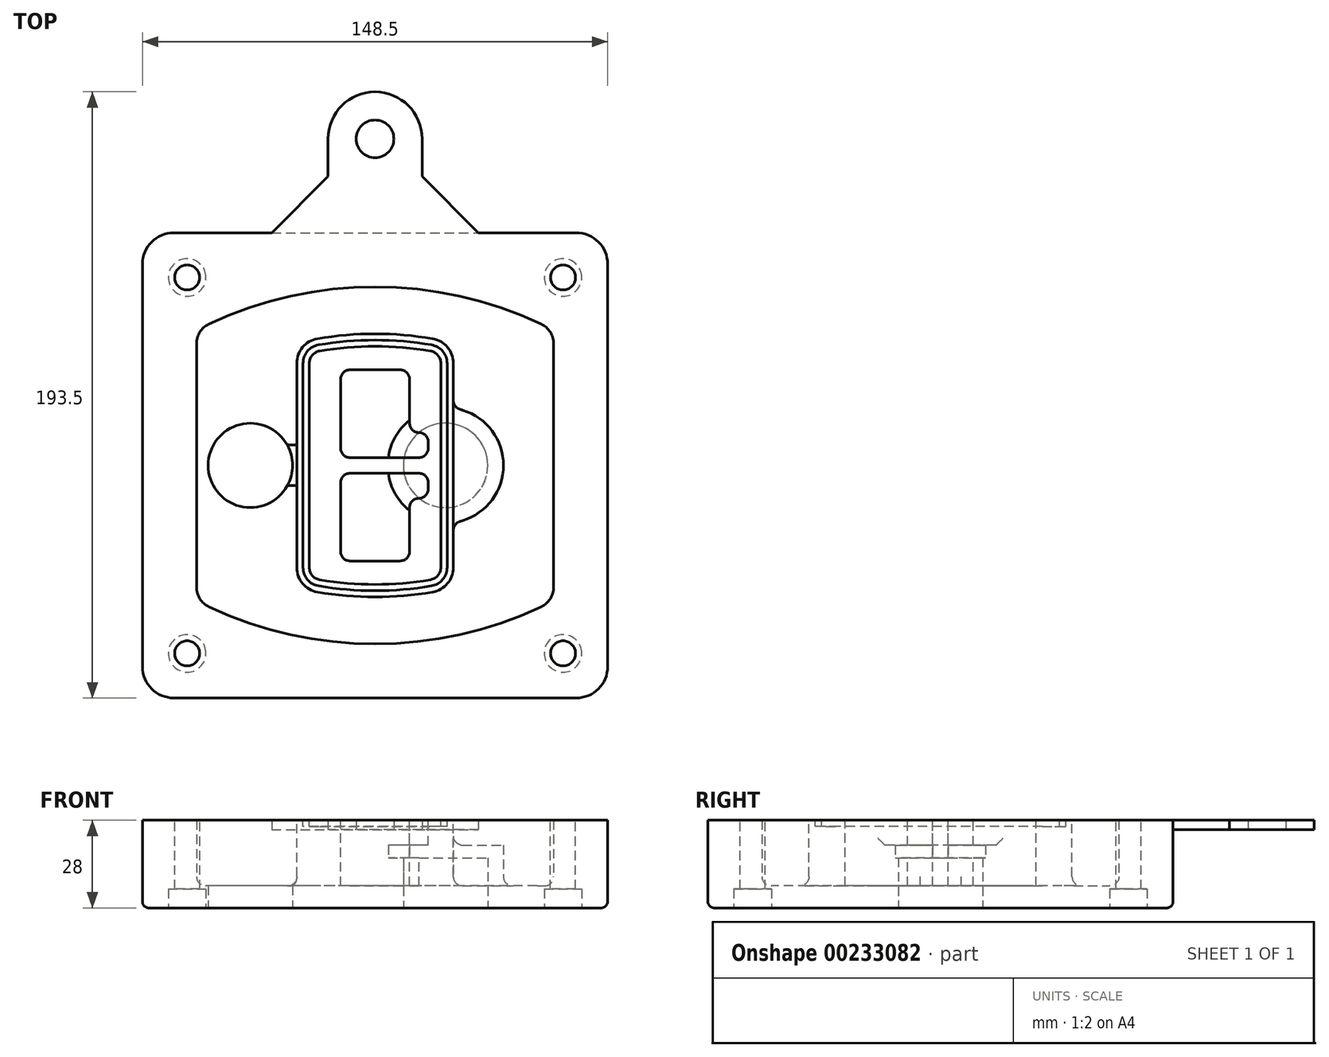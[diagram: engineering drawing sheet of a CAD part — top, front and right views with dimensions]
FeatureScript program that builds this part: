
annotation { "Feature Type Name" : "Feature", "Feature Type Description" : "" }
export const myFeature = defineFeature(function(context is Context, id is Id, definition is map)
    precondition{}
    {
        {
            var Q0;
            Q0=qCreatedBy(makeId("Top.planeOp"),FACE);
            var sketch = newSketch(context, id + "F0", { "sketchPlane" : qUnion([Q0])});
            skPoint(sketch, "E0.rect.middle", {"position": v(0, 0) * mm});
            skLineSegment(sketch, "E1.bottom", {"start": v(-64.25, -74.25) * mm, "end": v(64.25, -74.25) * mm});
            skLineSegment(sketch, "E1.top", {"start": v(-64.25, 74.25) * mm, "end": v(64.25, 74.25) * mm});
            skLineSegment(sketch, "E1.left", {"start": v(-74.25, -64.25) * mm, "end": v(-74.25, 64.25) * mm});
            skLineSegment(sketch, "E1.right", {"start": v(74.25, -64.25) * mm, "end": v(74.25, 64.25) * mm});
            skLineSegment(sketch, "E2", {"start": v(-74.25, 74.25) * mm, "end": v(74.25, -74.25) * mm, "construction": true});
            skLineSegment(sketch, "E3", {"start": v(74.25, 74.25) * mm, "end": v(-74.25, -74.25) * mm, "construction": true});
            skCircle(sketch, "E4", {"center": v(-60, 60) * mm, "radius": 4 * mm});
            skCircle(sketch, "E5", {"center": v(60, 60) * mm, "radius": 4 * mm});
            skCircle(sketch, "E6", {"center": v(60, -60) * mm, "radius": 4 * mm});
            skCircle(sketch, "E7", {"center": v(-60, -60) * mm, "radius": 4 * mm});
            skLineSegment(sketch, "E8", {"start": v(-60, 60) * mm, "end": v(60, 60) * mm, "construction": true});
            skLineSegment(sketch, "E9", {"start": v(60, 60) * mm, "end": v(60, -60) * mm, "construction": true});
            skLineSegment(sketch, "E10", {"start": v(60, -60) * mm, "end": v(-60, -60) * mm, "construction": true});
            skLineSegment(sketch, "E11", {"start": v(-60, -60) * mm, "end": v(-60, 60) * mm, "construction": true});
            skLineSegment(sketch, "E12", {"start": v(-60, 38.83) * mm, "end": v(-60, -38.83) * mm});
            skLineSegment(sketch, "E13", {"start": v(60, 38.83) * mm, "end": v(60, -38.83) * mm});
            skArc(sketch, "E14", {"start": v(54.26, 47.88) * mm, "mid": v(0, 60) * mm, "end": v(-54.26, 47.88) * mm});
            skArc(sketch, "E15", {"start": v(-54.26, -47.88) * mm, "mid": v(0, -60) * mm, "end": v(54.26, -47.88) * mm});
            skLineSegment(sketch, "E16", {"start": v(-60, 0) * mm, "end": v(60, 0) * mm, "construction": true});
            skPoint(sketch, "E17.visualSharp", {"position": v(-60, -45) * mm});
            skArc(sketch, "E17.filletArc", {"start": v(-60, -38.83) * mm, "mid": v(-58.44, -44.2) * mm, "end": v(-54.26, -47.88) * mm});
            skPoint(sketch, "E18.visualSharp", {"position": v(-60, 45) * mm});
            skArc(sketch, "E18.filletArc", {"start": v(-54.26, 47.88) * mm, "mid": v(-58.44, 44.2) * mm, "end": v(-60, 38.83) * mm});
            skPoint(sketch, "E19.visualSharp", {"position": v(60, 45) * mm});
            skArc(sketch, "E19.filletArc", {"start": v(60, 38.83) * mm, "mid": v(58.44, 44.2) * mm, "end": v(54.26, 47.88) * mm});
            skPoint(sketch, "E20.visualSharp", {"position": v(60, -45) * mm});
            skArc(sketch, "E20.filletArc", {"start": v(54.26, -47.88) * mm, "mid": v(58.44, -44.2) * mm, "end": v(60, -38.83) * mm});
            skPoint(sketch, "E21.visualSharp", {"position": v(-74.25, 74.25) * mm});
            skArc(sketch, "E21.filletArc", {"start": v(-64.25, 74.25) * mm, "mid": v(-71.32, 71.32) * mm, "end": v(-74.25, 64.25) * mm});
            skPoint(sketch, "E22.visualSharp", {"position": v(74.25, 74.25) * mm});
            skArc(sketch, "E22.filletArc", {"start": v(74.25, 64.25) * mm, "mid": v(71.32, 71.32) * mm, "end": v(64.25, 74.25) * mm});
            skPoint(sketch, "E23.visualSharp", {"position": v(74.25, -74.25) * mm});
            skArc(sketch, "E23.filletArc", {"start": v(64.25, -74.25) * mm, "mid": v(71.32, -71.32) * mm, "end": v(74.25, -64.25) * mm});
            skPoint(sketch, "E24.visualSharp", {"position": v(-74.25, -74.25) * mm});
            skArc(sketch, "E24.filletArc", {"start": v(-74.25, -64.25) * mm, "mid": v(-71.32, -71.32) * mm, "end": v(-64.25, -74.25) * mm});
            skArc(sketch, "E25.0", {"start": v(57, 38.83) * mm, "mid": v(55.9, 42.58) * mm, "end": v(52.98, 45.17) * mm});
            skLineSegment(sketch, "E25.1", {"start": v(57, 38.83) * mm, "end": v(57, -38.83) * mm});
            skArc(sketch, "E25.2", {"start": v(52.98, -45.17) * mm, "mid": v(55.9, -42.58) * mm, "end": v(57, -38.83) * mm});
            skArc(sketch, "E25.3", {"start": v(-52.98, -45.17) * mm, "mid": v(0, -57) * mm, "end": v(52.98, -45.17) * mm});
            skArc(sketch, "E25.4", {"start": v(-57, -38.83) * mm, "mid": v(-55.9, -42.58) * mm, "end": v(-52.98, -45.17) * mm});
            skArc(sketch, "E25.5", {"start": v(52.98, 45.17) * mm, "mid": v(0, 57) * mm, "end": v(-52.98, 45.17) * mm});
            skLineSegment(sketch, "E25.6", {"start": v(-57, 38.83) * mm, "end": v(-57, -38.83) * mm});
            skArc(sketch, "E25.7", {"start": v(-52.98, 45.17) * mm, "mid": v(-55.9, 42.58) * mm, "end": v(-57, 38.83) * mm});
            skArc(sketch, "E26.0", {"start": v(-55.96, 51.5) * mm, "mid": v(-61.82, 46.33) * mm, "end": v(-64, 38.83) * mm});
            skArc(sketch, "E26.1", {"start": v(55.96, 51.5) * mm, "mid": v(0, 64) * mm, "end": v(-55.96, 51.5) * mm});
            skArc(sketch, "E26.2", {"start": v(64, 38.83) * mm, "mid": v(61.82, 46.33) * mm, "end": v(55.96, 51.5) * mm});
            skLineSegment(sketch, "E26.3", {"start": v(64, 38.83) * mm, "end": v(64, -38.83) * mm});
            skArc(sketch, "E26.4", {"start": v(55.96, -51.5) * mm, "mid": v(61.82, -46.33) * mm, "end": v(64, -38.83) * mm});
            skLineSegment(sketch, "E26.5", {"start": v(-64, 38.83) * mm, "end": v(-64, -38.83) * mm});
            skArc(sketch, "E26.6", {"start": v(-55.96, -51.5) * mm, "mid": v(0, -64) * mm, "end": v(55.96, -51.5) * mm});
            skArc(sketch, "E26.7", {"start": v(-64, -38.83) * mm, "mid": v(-61.82, -46.33) * mm, "end": v(-55.96, -51.5) * mm});
            skSolve(sketch);
        }
        {
            var Q0;
            Q0=makeQuery(id+"F0.imprint","IMPRINT",FACE,{"disambiguationData":[TD([[makeQuery(id+"F0.imprint","IMPRINT",EDGE,{"derivedFrom":sQuery(id+"F0.wireOp",EDGE,"E1.bottom")}),1.0]])]});
            var Q1;
            Q1=makeQuery(id+"F0.imprint","IMPRINT",FACE,{"disambiguationData":[TD([[makeQuery(id+"F0.imprint","IMPRINT",EDGE,{"derivedFrom":sQuery(id+"F0.wireOp",EDGE,"E12")}),1.0]])]});
            var Q2;
            Q2=makeQuery(id+"F0.imprint","IMPRINT",FACE,{"disambiguationData":[TD([[makeQuery(id+"F0.imprint","IMPRINT",EDGE,{"derivedFrom":sQuery(id+"F0.wireOp",EDGE,"E25.0")}),1.0]])]});
            var Q3;
            Q3=makeQuery(id+"F0.imprint","IMPRINT",FACE,{"disambiguationData":[TD([[makeQuery(id+"F0.imprint","IMPRINT",EDGE,{"derivedFrom":sQuery(id+"F0.wireOp",EDGE,"E12")}),-1.0]])]});
            extrude(context, id + "F1", {"entities" : qUnion([Q0, Q1, Q2, Q3]), "oppositeDirection" : true, "depth" : 25 * mm});
        }
        {
            var Q0;
            Q0=makeQuery(id+"F0.imprint","IMPRINT",FACE,{"disambiguationData":[TD([[makeQuery(id+"F0.imprint","IMPRINT",EDGE,{"derivedFrom":sQuery(id+"F0.wireOp",EDGE,"E12")}),1.0]])]});
            extrude(context, id + "F2", {"entities" : qUnion([Q0]), "operationType" : NewBodyOperationType.ADD, "depth" : 3 * mm});
        }
        {
            var Q0;
            Q0=makeQuery(id+"F0.imprint","IMPRINT",FACE,{"disambiguationData":[TD([[makeQuery(id+"F0.imprint","IMPRINT",EDGE,{"derivedFrom":sQuery(id+"F0.wireOp",EDGE,"E25.0")}),1.0]])]});
            extrude(context, id + "F3", {"entities" : qUnion([Q0]), "operationType" : NewBodyOperationType.REMOVE, "oppositeDirection" : true, "depth" : 18 * mm});
        }
        {
            var Q0;
            Q0=makeQuery(id+"F2.opExtrude","CAP_FACE",FACE,{"disambiguationData":[OSD([sQuery(id+"F0.wireOp",EDGE,"E12"),sQuery(id+"F0.wireOp",EDGE,"E13"),sQuery(id+"F0.wireOp",EDGE,"E14"),sQuery(id+"F0.wireOp",EDGE,"E15"),sQuery(id+"F0.wireOp",EDGE,"E17.filletArc"),sQuery(id+"F0.wireOp",EDGE,"E18.filletArc"),sQuery(id+"F0.wireOp",EDGE,"E19.filletArc"),sQuery(id+"F0.wireOp",EDGE,"E20.filletArc"),sQuery(id+"F0.wireOp",EDGE,"E25.0"),sQuery(id+"F0.wireOp",EDGE,"E25.1"),sQuery(id+"F0.wireOp",EDGE,"E25.2"),sQuery(id+"F0.wireOp",EDGE,"E25.3"),sQuery(id+"F0.wireOp",EDGE,"E25.4"),sQuery(id+"F0.wireOp",EDGE,"E25.5"),sQuery(id+"F0.wireOp",EDGE,"E25.6"),sQuery(id+"F0.wireOp",EDGE,"E25.7")])],"isStart":false});
            var sketch = newSketch(context, id + "F4", { "sketchPlane" : qUnion([Q0])});
            skArc(sketch, "E27.0", {"start": v(-18.34, -40.45) * mm, "mid": v(0, -42) * mm, "end": v(18.34, -40.45) * mm});
            skArc(sketch, "E28.0", {"start": v(18.34, 40.45) * mm, "mid": v(0, 42) * mm, "end": v(-18.34, 40.45) * mm});
            skLineSegment(sketch, "E29", {"start": v(-25, 32.57) * mm, "end": v(-25, -32.57) * mm});
            skLineSegment(sketch, "E30", {"start": v(25, 32.57) * mm, "end": v(25, -32.57) * mm});
            skLineSegment(sketch, "E31", {"start": v(-25, 39.1) * mm, "end": v(25, 39.1) * mm, "construction": true});
            skLineSegment(sketch, "E32", {"start": v(-25, -39.1) * mm, "end": v(25, -39.1) * mm, "construction": true});
            skPoint(sketch, "E33.visualSharp", {"position": v(-25, 39.1) * mm});
            skArc(sketch, "E33.filletArc", {"start": v(-18.34, 40.45) * mm, "mid": v(-23.11, 37.73) * mm, "end": v(-25, 32.57) * mm});
            skPoint(sketch, "E34.visualSharp", {"position": v(25, 39.1) * mm});
            skArc(sketch, "E34.filletArc", {"start": v(25, 32.57) * mm, "mid": v(23.11, 37.73) * mm, "end": v(18.34, 40.45) * mm});
            skPoint(sketch, "E35.visualSharp", {"position": v(25, -39.1) * mm});
            skArc(sketch, "E35.filletArc", {"start": v(18.34, -40.45) * mm, "mid": v(23.11, -37.73) * mm, "end": v(25, -32.57) * mm});
            skPoint(sketch, "E36.visualSharp", {"position": v(-25, -39.1) * mm});
            skArc(sketch, "E36.filletArc", {"start": v(-25, -32.57) * mm, "mid": v(-23.11, -37.73) * mm, "end": v(-18.34, -40.45) * mm});
            skArc(sketch, "E37.0", {"start": v(52.98, 45.17) * mm, "mid": v(0, 57) * mm, "end": v(-52.98, 45.17) * mm});
            skArc(sketch, "E37.1", {"start": v(-52.98, 45.17) * mm, "mid": v(-55.9, 42.58) * mm, "end": v(-57, 38.83) * mm});
            skLineSegment(sketch, "E37.2", {"start": v(-57, 38.83) * mm, "end": v(-57, -38.83) * mm});
            skArc(sketch, "E37.3", {"start": v(-57, -38.83) * mm, "mid": v(-55.9, -42.58) * mm, "end": v(-52.98, -45.17) * mm});
            skArc(sketch, "E37.4", {"start": v(-52.98, -45.17) * mm, "mid": v(0, -57) * mm, "end": v(52.98, -45.17) * mm});
            skArc(sketch, "E37.5", {"start": v(52.98, -45.17) * mm, "mid": v(55.9, -42.58) * mm, "end": v(57, -38.83) * mm});
            skLineSegment(sketch, "E37.6", {"start": v(57, 38.83) * mm, "end": v(57, -38.83) * mm});
            skArc(sketch, "E37.7", {"start": v(57, 38.83) * mm, "mid": v(55.9, 42.58) * mm, "end": v(52.98, 45.17) * mm});
            skLineSegment(sketch, "E38.0", {"start": v(23, 32.57) * mm, "end": v(23, -32.57) * mm});
            skArc(sketch, "E38.1", {"start": v(18, -38.48) * mm, "mid": v(21.58, -36.44) * mm, "end": v(23, -32.57) * mm});
            skArc(sketch, "E38.2", {"start": v(-18, -38.48) * mm, "mid": v(0, -40) * mm, "end": v(18, -38.48) * mm});
            skArc(sketch, "E38.3", {"start": v(-23, -32.57) * mm, "mid": v(-21.58, -36.44) * mm, "end": v(-18, -38.48) * mm});
            skLineSegment(sketch, "E38.4", {"start": v(-23, 32.57) * mm, "end": v(-23, -32.57) * mm});
            skArc(sketch, "E38.5", {"start": v(23, 32.57) * mm, "mid": v(21.58, 36.44) * mm, "end": v(18, 38.48) * mm});
            skArc(sketch, "E38.6", {"start": v(-18, 38.48) * mm, "mid": v(-21.58, 36.44) * mm, "end": v(-23, 32.57) * mm});
            skArc(sketch, "E38.7", {"start": v(18, 38.48) * mm, "mid": v(0, 40) * mm, "end": v(-18, 38.48) * mm});
            skArc(sketch, "E39.0", {"start": v(21, 32.57) * mm, "mid": v(20.06, 35.15) * mm, "end": v(17.67, 36.5) * mm});
            skLineSegment(sketch, "E39.1", {"start": v(21, 32.57) * mm, "end": v(21, -32.57) * mm});
            skArc(sketch, "E39.2", {"start": v(17.67, -36.5) * mm, "mid": v(20.06, -35.15) * mm, "end": v(21, -32.57) * mm});
            skArc(sketch, "E39.3", {"start": v(-17.67, -36.5) * mm, "mid": v(0, -38) * mm, "end": v(17.67, -36.5) * mm});
            skArc(sketch, "E39.4", {"start": v(-21, -32.57) * mm, "mid": v(-20.06, -35.15) * mm, "end": v(-17.67, -36.5) * mm});
            skArc(sketch, "E39.5", {"start": v(17.67, 36.5) * mm, "mid": v(0, 38) * mm, "end": v(-17.67, 36.5) * mm});
            skLineSegment(sketch, "E39.6", {"start": v(-21, 32.57) * mm, "end": v(-21, -32.57) * mm});
            skArc(sketch, "E39.7", {"start": v(-17.67, 36.5) * mm, "mid": v(-20.06, 35.15) * mm, "end": v(-21, 32.57) * mm});
            skLineSegment(sketch, "E40", {"start": v(-25, 0) * mm, "end": v(25, 0) * mm, "construction": true});
            skLineSegment(sketch, "E41", {"start": v(-11, 5.5) * mm, "end": v(-11, 27.5) * mm});
            skLineSegment(sketch, "E42", {"start": v(-8, 30.5) * mm, "end": v(8, 30.5) * mm});
            skLineSegment(sketch, "E43", {"start": v(11, 27.5) * mm, "end": v(11, 13.5) * mm});
            skLineSegment(sketch, "E44", {"start": v(14, 10.5) * mm, "end": v(14, 10.5) * mm});
            skLineSegment(sketch, "E45", {"start": v(17, 7.5) * mm, "end": v(17, 5.5) * mm});
            skLineSegment(sketch, "E46", {"start": v(14, 2.5) * mm, "end": v(-8, 2.5) * mm});
            skPoint(sketch, "E47.visualSharp", {"position": v(-11, 30.5) * mm});
            skArc(sketch, "E47.filletArc", {"start": v(-8, 30.5) * mm, "mid": v(-10.12, 29.62) * mm, "end": v(-11, 27.5) * mm});
            skPoint(sketch, "E48.visualSharp", {"position": v(11, 30.5) * mm});
            skArc(sketch, "E48.filletArc", {"start": v(11, 27.5) * mm, "mid": v(10.12, 29.62) * mm, "end": v(8, 30.5) * mm});
            skPoint(sketch, "E49.visualSharp", {"position": v(11, 10.5) * mm});
            skArc(sketch, "E49.filletArc", {"start": v(11, 13.5) * mm, "mid": v(11.88, 11.38) * mm, "end": v(14, 10.5) * mm});
            skPoint(sketch, "E50.visualSharp", {"position": v(17, 10.5) * mm});
            skArc(sketch, "E50.filletArc", {"start": v(17, 7.5) * mm, "mid": v(16.12, 9.62) * mm, "end": v(14, 10.5) * mm});
            skPoint(sketch, "E51.visualSharp", {"position": v(17, 2.5) * mm});
            skArc(sketch, "E51.filletArc", {"start": v(14, 2.5) * mm, "mid": v(16.12, 3.38) * mm, "end": v(17, 5.5) * mm});
            skPoint(sketch, "E52.visualSharp", {"position": v(-11, 2.5) * mm});
            skArc(sketch, "E52.filletArc", {"start": v(-11, 5.5) * mm, "mid": v(-10.12, 3.38) * mm, "end": v(-8, 2.5) * mm});
            skLineSegment(sketch, "E53.0.MirrorCS", {"start": v(14, -2.5) * mm, "end": v(-8, -2.5) * mm});
            skArc(sketch, "E54.0.MirrorCS", {"start": v(-11, -5.5) * mm, "mid": v(-10.12, -3.38) * mm, "end": v(-8, -2.5) * mm});
            skLineSegment(sketch, "E55.0.MirrorCS", {"start": v(-11, -5.5) * mm, "end": v(-11, -27.5) * mm});
            skArc(sketch, "E56.0.MirrorCS", {"start": v(-8, -30.5) * mm, "mid": v(-10.12, -29.62) * mm, "end": v(-11, -27.5) * mm});
            skLineSegment(sketch, "E57.0.MirrorCS", {"start": v(-8, -30.5) * mm, "end": v(8, -30.5) * mm});
            skArc(sketch, "E58.0.MirrorCS", {"start": v(11, -27.5) * mm, "mid": v(10.12, -29.62) * mm, "end": v(8, -30.5) * mm});
            skLineSegment(sketch, "E59.0.MirrorCS", {"start": v(11, -27.5) * mm, "end": v(11, -13.5) * mm});
            skArc(sketch, "E60.0.MirrorCS", {"start": v(11, -13.5) * mm, "mid": v(11.88, -11.38) * mm, "end": v(14, -10.5) * mm});
            skArc(sketch, "E61.0.MirrorCS", {"start": v(17, -7.5) * mm, "mid": v(16.12, -9.62) * mm, "end": v(14, -10.5) * mm});
            skLineSegment(sketch, "E62.0.MirrorCS", {"start": v(17, -7.5) * mm, "end": v(17, -5.5) * mm});
            skArc(sketch, "E63.0.MirrorCS", {"start": v(14, -2.5) * mm, "mid": v(16.12, -3.38) * mm, "end": v(17, -5.5) * mm});
            skSolve(sketch);
        }
        {
            var Q0;
            Q0=makeQuery(id+"F4.imprint","IMPRINT",FACE,{"disambiguationData":[TD([[makeQuery(id+"F4.imprint","IMPRINT",EDGE,{"derivedFrom":sQuery(id+"F4.wireOp",EDGE,"E27.0")}),1.0]])]});
            var Q1;
            Q1=makeQuery(id+"F4.imprint","IMPRINT",FACE,{"disambiguationData":[TD([[makeQuery(id+"F4.imprint","IMPRINT",EDGE,{"derivedFrom":sQuery(id+"F4.wireOp",EDGE,"E38.0")}),-1.0]])]});
            var Q2;
            Q2=makeQuery(id+"F4.imprint","IMPRINT",FACE,{"disambiguationData":[TD([[makeQuery(id+"F4.imprint","IMPRINT",EDGE,{"derivedFrom":sQuery(id+"F4.wireOp",EDGE,"E39.0")}),1.0]])]});
            extrude(context, id + "F5", {"entities" : qUnion([Q0, Q1, Q2]), "operationType" : NewBodyOperationType.ADD, "endBound" : BoundingType.UP_TO_NEXT, "oppositeDirection" : true, "depth" : 25 * mm});
        }
        {
            var Q0;
            Q0=makeQuery(id+"F4.imprint","IMPRINT",FACE,{"disambiguationData":[TD([[makeQuery(id+"F4.imprint","IMPRINT",EDGE,{"derivedFrom":sQuery(id+"F4.wireOp",EDGE,"E38.0")}),-1.0]])]});
            extrude(context, id + "F6", {"entities" : qUnion([Q0]), "operationType" : NewBodyOperationType.REMOVE, "oppositeDirection" : true, "depth" : 2 * mm});
        }
        {
            var Q0;
            Q0=makeQuery(id+"F1.opExtrude","CAP_FACE",FACE,{"disambiguationData":[OSD([sQuery(id+"F0.wireOp",EDGE,"E1.bottom"),sQuery(id+"F0.wireOp",EDGE,"E1.top"),sQuery(id+"F0.wireOp",EDGE,"E1.left"),sQuery(id+"F0.wireOp",EDGE,"E1.right"),sQuery(id+"F0.wireOp",EDGE,"E4"),sQuery(id+"F0.wireOp",EDGE,"E5"),sQuery(id+"F0.wireOp",EDGE,"E6"),sQuery(id+"F0.wireOp",EDGE,"E7"),sQuery(id+"F0.wireOp",EDGE,"E21.filletArc"),sQuery(id+"F0.wireOp",EDGE,"E22.filletArc"),sQuery(id+"F0.wireOp",EDGE,"E23.filletArc"),sQuery(id+"F0.wireOp",EDGE,"E24.filletArc")])],"isStart":false});
            var sketch = newSketch(context, id + "F7", { "sketchPlane" : qUnion([Q0])});
            skCircle(sketch, "E64", {"center": v(22.5, 0) * mm, "radius": 13.47 * mm});
            skCircle(sketch, "E65", {"center": v(-39.81, 0) * mm, "radius": 13.47 * mm});
            skLineSegment(sketch, "E66", {"start": v(74.25, 0) * mm, "end": v(-74.25, 0) * mm});
            skCircle(sketch, "E67", {"center": v(22.5, 0) * mm, "radius": 18.47 * mm});
            skCircle(sketch, "E68", {"center": v(60, -60) * mm, "radius": 6 * mm});
            skCircle(sketch, "E69", {"center": v(-60, -60) * mm, "radius": 6 * mm});
            skCircle(sketch, "E70", {"center": v(-60, 60) * mm, "radius": 6 * mm});
            skCircle(sketch, "E71", {"center": v(60, 60) * mm, "radius": 6 * mm});
            skSolve(sketch);
        }
        {
            var Q0;
            {var subQ1=sQuery(id+"F7.wireOp",EDGE,"E66");var subQ4=sQuery(id+"F7.wireOp",EDGE,"E64");var subQ6=makeQuery(id+"F7.imprint","INTERSECT",VERTEX,{"disambiguationData":[OD(0.0)],"derivedFrom":[subQ4,subQ1]});Q0=makeQuery(id+"F7.imprint","IMPRINT",FACE,{"disambiguationData":[TD([[makeQuery(id+"F7.imprint","IMPRINT",EDGE,{"disambiguationData":[TD([[subQ6,-1.0]])],"derivedFrom":subQ4}),-1.0]])]});}
            var Q1;
            {var subQ0=sQuery(id+"F7.wireOp",EDGE,"E66");var subQ1=sQuery(id+"F7.wireOp",EDGE,"E64");var subQ3=makeQuery(id+"F7.imprint","INTERSECT",VERTEX,{"disambiguationData":[OD(0.0)],"derivedFrom":[subQ1,subQ0]});Q1=makeQuery(id+"F7.imprint","IMPRINT",FACE,{"disambiguationData":[TD([[makeQuery(id+"F7.imprint","IMPRINT",EDGE,{"disambiguationData":[TD([[subQ3,-1.0]])],"derivedFrom":subQ1}),1.0]])]});}
            var Q2;
            {var subQ0=sQuery(id+"F7.wireOp",EDGE,"E66");var subQ1=sQuery(id+"F7.wireOp",EDGE,"E64");var subQ3=makeQuery(id+"F7.imprint","INTERSECT",VERTEX,{"disambiguationData":[OD(0.0)],"derivedFrom":[subQ1,subQ0]});Q2=makeQuery(id+"F7.imprint","IMPRINT",FACE,{"disambiguationData":[TD([[makeQuery(id+"F7.imprint","IMPRINT",EDGE,{"disambiguationData":[TD([[subQ3,1.0]])],"derivedFrom":subQ1}),1.0]])]});}
            var Q3;
            {var subQ1=sQuery(id+"F7.wireOp",EDGE,"E66");var subQ4=sQuery(id+"F7.wireOp",EDGE,"E64");var subQ6=makeQuery(id+"F7.imprint","INTERSECT",VERTEX,{"disambiguationData":[OD(0.0)],"derivedFrom":[subQ4,subQ1]});Q3=makeQuery(id+"F7.imprint","IMPRINT",FACE,{"disambiguationData":[TD([[makeQuery(id+"F7.imprint","IMPRINT",EDGE,{"disambiguationData":[TD([[subQ6,1.0]])],"derivedFrom":subQ4}),-1.0]])]});}
            extrude(context, id + "F8", {"entities" : qUnion([Q0, Q1, Q2, Q3]), "operationType" : NewBodyOperationType.ADD, "oppositeDirection" : true, "depth" : 20 * mm});
        }
        {
            var Q0;
            {var subQ0=sQuery(id+"F7.wireOp",EDGE,"E66");var subQ1=sQuery(id+"F7.wireOp",EDGE,"E64");var subQ3=makeQuery(id+"F7.imprint","INTERSECT",VERTEX,{"disambiguationData":[OD(0.0)],"derivedFrom":[subQ1,subQ0]});Q0=makeQuery(id+"F7.imprint","IMPRINT",FACE,{"disambiguationData":[TD([[makeQuery(id+"F7.imprint","IMPRINT",EDGE,{"disambiguationData":[TD([[subQ3,-1.0]])],"derivedFrom":subQ1}),1.0]])]});}
            var Q1;
            {var subQ0=sQuery(id+"F7.wireOp",EDGE,"E66");var subQ1=sQuery(id+"F7.wireOp",EDGE,"E64");var subQ3=makeQuery(id+"F7.imprint","INTERSECT",VERTEX,{"disambiguationData":[OD(0.0)],"derivedFrom":[subQ1,subQ0]});Q1=makeQuery(id+"F7.imprint","IMPRINT",FACE,{"disambiguationData":[TD([[makeQuery(id+"F7.imprint","IMPRINT",EDGE,{"disambiguationData":[TD([[subQ3,1.0]])],"derivedFrom":subQ1}),1.0]])]});}
            extrude(context, id + "F9", {"entities" : qUnion([Q0, Q1]), "operationType" : NewBodyOperationType.REMOVE, "oppositeDirection" : true, "depth" : 16 * mm});
        }
        {
            var Q0;
            {var subQ0=sQuery(id+"F7.wireOp",EDGE,"E66");var subQ1=sQuery(id+"F7.wireOp",EDGE,"E65");var subQ3=makeQuery(id+"F7.imprint","INTERSECT",VERTEX,{"disambiguationData":[OD(0.0)],"derivedFrom":[subQ1,subQ0]});Q0=makeQuery(id+"F7.imprint","IMPRINT",FACE,{"disambiguationData":[TD([[makeQuery(id+"F7.imprint","IMPRINT",EDGE,{"disambiguationData":[TD([[subQ3,-1.0]])],"derivedFrom":subQ1}),1.0]])]});}
            var Q1;
            {var subQ0=sQuery(id+"F7.wireOp",EDGE,"E66");var subQ1=sQuery(id+"F7.wireOp",EDGE,"E65");var subQ3=makeQuery(id+"F7.imprint","INTERSECT",VERTEX,{"disambiguationData":[OD(0.0)],"derivedFrom":[subQ1,subQ0]});Q1=makeQuery(id+"F7.imprint","IMPRINT",FACE,{"disambiguationData":[TD([[makeQuery(id+"F7.imprint","IMPRINT",EDGE,{"disambiguationData":[TD([[subQ3,1.0]])],"derivedFrom":subQ1}),1.0]])]});}
            extrude(context, id + "F10", {"entities" : qUnion([Q0, Q1]), "operationType" : NewBodyOperationType.REMOVE, "oppositeDirection" : true, "depth" : 25 * mm});
        }
        {
            var Q0;
            Q0=makeQuery(id+"F7.imprint","IMPRINT",FACE,{"disambiguationData":[TD([[makeQuery(id+"F7.imprint","IMPRINT",EDGE,{"derivedFrom":sQuery(id+"F7.wireOp",EDGE,"E68")}),1.0]])]});
            var Q1;
            Q1=makeQuery(id+"F7.imprint","IMPRINT",FACE,{"disambiguationData":[TD([[makeQuery(id+"F7.imprint","IMPRINT",EDGE,{"derivedFrom":makeQuery(id+"F1.opExtrude","CAP_EDGE",EDGE,{"disambiguationData":[OSD([sQuery(id+"F0.wireOp",EDGE,"E5")])],"isStart":false})}),-1.0]])]});
            var Q2;
            Q2=makeQuery(id+"F7.imprint","IMPRINT",FACE,{"disambiguationData":[TD([[makeQuery(id+"F7.imprint","IMPRINT",EDGE,{"derivedFrom":sQuery(id+"F7.wireOp",EDGE,"E69")}),1.0]])]});
            var Q3;
            Q3=makeQuery(id+"F7.imprint","IMPRINT",FACE,{"disambiguationData":[TD([[makeQuery(id+"F7.imprint","IMPRINT",EDGE,{"derivedFrom":makeQuery(id+"F1.opExtrude","CAP_EDGE",EDGE,{"disambiguationData":[OSD([sQuery(id+"F0.wireOp",EDGE,"E4")])],"isStart":false})}),-1.0]])]});
            var Q4;
            Q4=makeQuery(id+"F7.imprint","IMPRINT",FACE,{"disambiguationData":[TD([[makeQuery(id+"F7.imprint","IMPRINT",EDGE,{"derivedFrom":sQuery(id+"F7.wireOp",EDGE,"E70")}),1.0]])]});
            var Q5;
            Q5=makeQuery(id+"F7.imprint","IMPRINT",FACE,{"disambiguationData":[TD([[makeQuery(id+"F7.imprint","IMPRINT",EDGE,{"derivedFrom":makeQuery(id+"F1.opExtrude","CAP_EDGE",EDGE,{"disambiguationData":[OSD([sQuery(id+"F0.wireOp",EDGE,"E7")])],"isStart":false})}),-1.0]])]});
            var Q6;
            Q6=makeQuery(id+"F7.imprint","IMPRINT",FACE,{"disambiguationData":[TD([[makeQuery(id+"F7.imprint","IMPRINT",EDGE,{"derivedFrom":sQuery(id+"F7.wireOp",EDGE,"E71")}),1.0]])]});
            var Q7;
            Q7=makeQuery(id+"F7.imprint","IMPRINT",FACE,{"disambiguationData":[TD([[makeQuery(id+"F7.imprint","IMPRINT",EDGE,{"derivedFrom":makeQuery(id+"F1.opExtrude","CAP_EDGE",EDGE,{"disambiguationData":[OSD([sQuery(id+"F0.wireOp",EDGE,"E6")])],"isStart":false})}),-1.0]])]});
            extrude(context, id + "F11", {"entities" : qUnion([Q0, Q1, Q2, Q3, Q4, Q5, Q6, Q7]), "operationType" : NewBodyOperationType.REMOVE, "oppositeDirection" : true, "depth" : 6 * mm});
        }
        {
            var Q0;
            Q0=makeQuery(id+"F9.boolean.opBoolean","COPY",FACE,{"derivedFrom":makeQuery(id+"F9.opExtrude","CAP_FACE",FACE,{"disambiguationData":[OSD([sQuery(id+"F7.wireOp",EDGE,"E64")])],"isStart":false})});
            var sketch = newSketch(context, id + "F12", { "sketchPlane" : qUnion([Q0])});
            skArc(sketch, "E72.0", {"start": v(11, 14.45) * mm, "mid": v(6.45, 9.13) * mm, "end": v(4.2, 2.5) * mm});
            skArc(sketch, "E72.1", {"start": v(4.2, -2.5) * mm, "mid": v(6.45, -9.13) * mm, "end": v(11, -14.45) * mm});
            skLineSegment(sketch, "E73", {"start": v(4.2, -2.5) * mm, "end": v(14, -2.5) * mm});
            skLineSegment(sketch, "E74.0", {"start": v(14, 2.5) * mm, "end": v(4.2, 2.5) * mm});
            skArc(sketch, "E74.1", {"start": v(14, 2.5) * mm, "mid": v(16.12, 3.38) * mm, "end": v(17, 5.5) * mm});
            skLineSegment(sketch, "E74.2", {"start": v(17, 7.5) * mm, "end": v(17, 5.5) * mm});
            skArc(sketch, "E74.3", {"start": v(17, 7.5) * mm, "mid": v(16.12, 9.62) * mm, "end": v(14, 10.5) * mm});
            skArc(sketch, "E74.4", {"start": v(11, 13.5) * mm, "mid": v(11.88, 11.38) * mm, "end": v(14, 10.5) * mm});
            skLineSegment(sketch, "E74.5", {"start": v(11, 14.45) * mm, "end": v(11, 13.5) * mm});
            skLineSegment(sketch, "E74.7", {"start": v(14, -2.5) * mm, "end": v(4.2, -2.5) * mm});
            skArc(sketch, "E74.8", {"start": v(14, -2.5) * mm, "mid": v(16.12, -3.38) * mm, "end": v(17, -5.5) * mm});
            skLineSegment(sketch, "E74.9", {"start": v(17, -7.5) * mm, "end": v(17, -5.5) * mm});
            skArc(sketch, "E74.10", {"start": v(17, -7.5) * mm, "mid": v(16.12, -9.62) * mm, "end": v(14, -10.5) * mm});
            skArc(sketch, "E74.11", {"start": v(11, -13.5) * mm, "mid": v(11.88, -11.38) * mm, "end": v(14, -10.5) * mm});
            skLineSegment(sketch, "E74.12", {"start": v(11, -14.45) * mm, "end": v(11, -13.5) * mm});
            skPoint(sketch, "E75.orphan", {"position": v(11, -27.5) * mm});
            skPoint(sketch, "E76.orphan", {"position": v(-8, -2.5) * mm});
            skPoint(sketch, "E77.orphan", {"position": v(-8, 2.5) * mm});
            skPoint(sketch, "E78.orphan", {"position": v(11, 27.5) * mm});
            skSolve(sketch);
        }
        {
            var Q0;
            {var subQ7=sQuery(id+"F12.wireOp",EDGE,"E72.0");var subQ14=sQuery(id+"F12.wireOp",EDGE,"E72.1");var subQ16=sQuery(id+"F12.wireOp",EDGE,"E74.1");var subQ18=sQuery(id+"F12.wireOp",EDGE,"E74.8");Q0=qUnion([makeQuery(id+"F12.imprint","IMPRINT",FACE,{"disambiguationData":[TD([[makeQuery(id+"F12.imprint","IMPRINT",EDGE,{"derivedFrom":subQ7}),1.0]])]}),makeQuery(id+"F12.imprint","IMPRINT",FACE,{"disambiguationData":[TD([[makeQuery(id+"F12.imprint","IMPRINT",EDGE,{"derivedFrom":subQ14}),1.0]])]}),makeQuery(id+"F12.imprint","IMPRINT",FACE,{"disambiguationData":[TD([[makeQuery(id+"F12.imprint","IMPRINT",EDGE,{"derivedFrom":subQ16}),1.0]])]}),makeQuery(id+"F12.imprint","IMPRINT",FACE,{"disambiguationData":[TD([[makeQuery(id+"F12.imprint","IMPRINT",EDGE,{"derivedFrom":subQ18}),-1.0]])]})]);}
            var Q1;
            Q1=makeQuery(id+"F5.boolean.opBoolean","SPLIT",FACE,{"disambiguationData":[TD([makeQuery(id+"F5.opExtrude","SWEPT_FACE",FACE,{"disambiguationData":[OSD([sQuery(id+"F4.wireOp",EDGE,"E41")])]})])],"derivedFrom":makeQuery(id+"F3.boolean.opBoolean","COPY",FACE,{"derivedFrom":makeQuery(id+"F3.opExtrude","CAP_FACE",FACE,{"disambiguationData":[OSD([sQuery(id+"F0.wireOp",EDGE,"E25.0"),sQuery(id+"F0.wireOp",EDGE,"E25.1"),sQuery(id+"F0.wireOp",EDGE,"E25.2"),sQuery(id+"F0.wireOp",EDGE,"E25.3"),sQuery(id+"F0.wireOp",EDGE,"E25.4"),sQuery(id+"F0.wireOp",EDGE,"E25.5"),sQuery(id+"F0.wireOp",EDGE,"E25.6"),sQuery(id+"F0.wireOp",EDGE,"E25.7")])],"isStart":false})})});
            extrude(context, id + "F13", {"entities" : qUnion([Q0]), "operationType" : NewBodyOperationType.REMOVE, "endBound" : BoundingType.UP_TO_SURFACE, "endBoundEntityFace" : qUnion([Q1]), "depth" : 25 * mm});
        }
        {
            var Q0;
            Q0=makeQuery(id+"F3.boolean.opBoolean","COPY",EDGE,{"derivedFrom":makeQuery(id+"F3.opExtrude","CAP_EDGE",EDGE,{"disambiguationData":[OSD([sQuery(id+"F0.wireOp",EDGE,"E25.6")])],"isStart":false})});
            var Q1;
            Q1=makeQuery(id+"F8.boolean.opBoolean","INTERSECT",EDGE,{"derivedFrom":[makeQuery(id+"F5.opExtrude","SWEPT_FACE",FACE,{"disambiguationData":[OSD([sQuery(id+"F4.wireOp",EDGE,"E30")])]}),makeQuery(id+"F8.opExtrude","CAP_FACE",FACE,{"disambiguationData":[OSD([sQuery(id+"F7.wireOp",EDGE,"E67")])],"isStart":false})]});
            var Q2;
            Q2=makeQuery(id+"F8.boolean.opBoolean","INTERSECT",EDGE,{"disambiguationData":[OD(1.0)],"derivedFrom":[makeQuery(id+"F5.opExtrude","SWEPT_FACE",FACE,{"disambiguationData":[OSD([sQuery(id+"F4.wireOp",EDGE,"E30")])]}),makeQuery(id+"F8.opExtrude","SWEPT_FACE",FACE,{"disambiguationData":[OSD([sQuery(id+"F7.wireOp",EDGE,"E67")])]})]});
            var Q3;
            {var subQ0=sQuery(id+"F4.wireOp",EDGE,"E30");Q3=makeQuery(id+"F8.boolean.opBoolean","SPLIT",EDGE,{"disambiguationData":[TD([makeQuery(id+"F5.opExtrude","SWEPT_FACE",FACE,{"disambiguationData":[OSD([sQuery(id+"F4.wireOp",EDGE,"E35.filletArc")])]})])],"derivedFrom":makeQuery(id+"F5.opExtrude","CAP_EDGE",EDGE,{"disambiguationData":[OSD([subQ0])],"isStart":false})});}
            var Q4;
            {var subQ0=sQuery(id+"F0.wireOp",EDGE,"E25.7");var subQ1=sQuery(id+"F0.wireOp",EDGE,"E25.1");var subQ2=sQuery(id+"F0.wireOp",EDGE,"E25.6");var subQ3=sQuery(id+"F0.wireOp",EDGE,"E25.5");var subQ4=sQuery(id+"F0.wireOp",EDGE,"E25.4");var subQ5=sQuery(id+"F0.wireOp",EDGE,"E25.0");var subQ6=sQuery(id+"F0.wireOp",EDGE,"E25.2");var subQ7=sQuery(id+"F0.wireOp",EDGE,"E25.3");Q4=makeQuery(id+"F8.boolean.opBoolean","INTERSECT",EDGE,{"derivedFrom":[makeQuery(id+"F5.boolean.opBoolean","SPLIT",FACE,{"disambiguationData":[TD([makeQuery(id+"F2.opExtrude","SWEPT_FACE",FACE,{"disambiguationData":[OSD([subQ5])]})])],"derivedFrom":makeQuery(id+"F3.boolean.opBoolean","COPY",FACE,{"derivedFrom":makeQuery(id+"F3.opExtrude","CAP_FACE",FACE,{"disambiguationData":[OSD([subQ5,subQ1,subQ6,subQ7,subQ4,subQ3,subQ2,subQ0])],"isStart":false})})}),makeQuery(id+"F8.opExtrude","SWEPT_FACE",FACE,{"disambiguationData":[OSD([sQuery(id+"F7.wireOp",EDGE,"E67")])]})]});}
            var Q5;
            Q5=makeQuery(id+"F8.boolean.opBoolean","INTERSECT",EDGE,{"disambiguationData":[OD(0.0)],"derivedFrom":[makeQuery(id+"F5.opExtrude","SWEPT_FACE",FACE,{"disambiguationData":[OSD([sQuery(id+"F4.wireOp",EDGE,"E30")])]}),makeQuery(id+"F8.opExtrude","SWEPT_FACE",FACE,{"disambiguationData":[OSD([sQuery(id+"F7.wireOp",EDGE,"E67")])]})]});
            fillet(context, id + "F14", {"entities" : qUnion([Q0, Q1, Q2, Q3, Q4, Q5]), "radius" : 3 * mm, "tangentPropagation" : true, "allowEdgeOverflow" : false});
        }
        {
            var Q0;
            Q0=makeQuery(id+"F1.opExtrude","CAP_EDGE",EDGE,{"disambiguationData":[OSD([sQuery(id+"F0.wireOp",EDGE,"E1.bottom")])],"isStart":false});
            fillet(context, id + "F15", {"entities" : qUnion([Q0]), "radius" : 2 * mm, "tangentPropagation" : true, "allowEdgeOverflow" : false});
        }
        {
            var Q0;
            {var subQ0=sQuery(id+"F0.wireOp",EDGE,"E22.filletArc");var subQ1=sQuery(id+"F0.wireOp",EDGE,"E7");var subQ2=sQuery(id+"F0.wireOp",EDGE,"E6");var subQ3=sQuery(id+"F0.wireOp",EDGE,"E5");var subQ4=sQuery(id+"F0.wireOp",EDGE,"E4");var subQ5=sQuery(id+"F0.wireOp",EDGE,"E1.bottom");var subQ6=sQuery(id+"F0.wireOp",EDGE,"E21.filletArc");var subQ7=sQuery(id+"F0.wireOp",EDGE,"E1.top");var subQ8=sQuery(id+"F0.wireOp",EDGE,"E1.left");var subQ9=sQuery(id+"F0.wireOp",EDGE,"E1.right");var subQ10=sQuery(id+"F0.wireOp",EDGE,"E23.filletArc");var subQ11=sQuery(id+"F0.wireOp",EDGE,"E24.filletArc");Q0=makeQuery(id+"F2.boolean.opBoolean","SPLIT",FACE,{"disambiguationData":[TD([makeQuery(id+"F1.opExtrude","SWEPT_FACE",FACE,{"disambiguationData":[OSD([subQ5])]})])],"derivedFrom":makeQuery(id+"F1.opExtrude","CAP_FACE",FACE,{"disambiguationData":[OSD([subQ5,subQ7,subQ8,subQ9,subQ4,subQ3,subQ2,subQ1,subQ6,subQ0,subQ10,subQ11])],"isStart":true})});}
            var sketch = newSketch(context, id + "F16", { "sketchPlane" : qUnion([Q0])});
            skLineSegment(sketch, "E79.0", {"start": v(-60, 38.83) * mm, "end": v(-60, -38.83) * mm});
            skArc(sketch, "E79.1", {"start": v(-54.26, -47.88) * mm, "mid": v(0, -60) * mm, "end": v(54.26, -47.88) * mm});
            skArc(sketch, "E79.2", {"start": v(-60, -38.83) * mm, "mid": v(-58.44, -44.2) * mm, "end": v(-54.26, -47.88) * mm});
            skArc(sketch, "E79.3", {"start": v(-54.26, 47.88) * mm, "mid": v(-58.44, 44.2) * mm, "end": v(-60, 38.83) * mm});
            skArc(sketch, "E79.4", {"start": v(54.26, 47.88) * mm, "mid": v(0, 60) * mm, "end": v(-54.26, 47.88) * mm});
            skLineSegment(sketch, "E79.5", {"start": v(60, 38.83) * mm, "end": v(60, -38.83) * mm});
            skArc(sketch, "E79.6", {"start": v(60, 38.83) * mm, "mid": v(58.44, 44.2) * mm, "end": v(54.26, 47.88) * mm});
            skArc(sketch, "E79.7", {"start": v(54.26, -47.88) * mm, "mid": v(58.44, -44.2) * mm, "end": v(60, -38.83) * mm});
            skLineSegment(sketch, "E79.8", {"start": v(74.25, -64.25) * mm, "end": v(74.25, 64.25) * mm});
            skArc(sketch, "E79.9", {"start": v(74.25, 64.25) * mm, "mid": v(71.32, 71.32) * mm, "end": v(64.25, 74.25) * mm});
            skLineSegment(sketch, "E79.10", {"start": v(-64.25, 74.25) * mm, "end": v(64.25, 74.25) * mm});
            skArc(sketch, "E79.11", {"start": v(-64.25, 74.25) * mm, "mid": v(-71.32, 71.32) * mm, "end": v(-74.25, 64.25) * mm});
            skLineSegment(sketch, "E79.12", {"start": v(-74.25, -64.25) * mm, "end": v(-74.25, 64.25) * mm});
            skLineSegment(sketch, "E79.13", {"start": v(-64.25, -74.25) * mm, "end": v(64.25, -74.25) * mm});
            skArc(sketch, "E79.14", {"start": v(-74.25, -64.25) * mm, "mid": v(-71.32, -71.32) * mm, "end": v(-64.25, -74.25) * mm});
            skArc(sketch, "E79.15", {"start": v(64.25, -74.25) * mm, "mid": v(71.32, -71.32) * mm, "end": v(74.25, -64.25) * mm});
            skCircle(sketch, "E79.16", {"center": v(60, -60) * mm, "radius": 4 * mm});
            skCircle(sketch, "E79.17", {"center": v(-60, -60) * mm, "radius": 4 * mm});
            skCircle(sketch, "E79.18", {"center": v(-60, 60) * mm, "radius": 4 * mm});
            skCircle(sketch, "E79.19", {"center": v(60, 60) * mm, "radius": 4 * mm});
            skLineSegment(sketch, "E80", {"start": v(0, 74.25) * mm, "end": v(0, 104.25) * mm});
            skCircle(sketch, "E81", {"center": v(0, 104.25) * mm, "radius": 6 * mm});
            skLineSegment(sketch, "E82", {"start": v(-33, 74.25) * mm, "end": v(-15, 92.25) * mm});
            skLineSegment(sketch, "E83", {"start": v(33, 74.25) * mm, "end": v(15, 92.25) * mm});
            skLineSegment(sketch, "E84", {"start": v(-15, 92.25) * mm, "end": v(-15, 104.25) * mm});
            skLineSegment(sketch, "E85", {"start": v(15, 92.25) * mm, "end": v(15, 104.25) * mm});
            skArc(sketch, "E86", {"start": v(15, 104.25) * mm, "mid": v(0, 119.25) * mm, "end": v(-15, 104.25) * mm});
            skLineSegment(sketch, "E87", {"start": v(-74.25, 0) * mm, "end": v(74.25, 0) * mm, "construction": true});
            skArc(sketch, "E88.MirrorCS", {"start": v(15, -104.25) * mm, "mid": v(0, -119.25) * mm, "end": v(-15, -104.25) * mm});
            skLineSegment(sketch, "E89.MirrorCS", {"start": v(-15, -92.25) * mm, "end": v(-15, -104.25) * mm});
            skLineSegment(sketch, "E90.MirrorCS", {"start": v(-33, -74.25) * mm, "end": v(-15, -92.25) * mm});
            skLineSegment(sketch, "E91.MirrorCS", {"start": v(0, -74.25) * mm, "end": v(0, -104.25) * mm});
            skLineSegment(sketch, "E92.MirrorCS", {"start": v(15, -92.25) * mm, "end": v(15, -104.25) * mm});
            skLineSegment(sketch, "E93.MirrorCS", {"start": v(33, -74.25) * mm, "end": v(15, -92.25) * mm});
            skCircle(sketch, "E94.MirrorC", {"center": v(0, -104.25) * mm, "radius": 6 * mm});
            skSolve(sketch);
        }
        {
            var Q0;
            Q0=makeQuery(id+"F16.imprint","IMPRINT",FACE,{"disambiguationData":[TD([[makeQuery(id+"F16.imprint","IMPRINT",EDGE,{"derivedFrom":sQuery(id+"F16.wireOp",EDGE,"E81")}),-1.0]])]});
            var Q1;
            Q1=makeQuery(id+"F16.imprint","IMPRINT",FACE,{"disambiguationData":[TD([[makeQuery(id+"F16.imprint","IMPRINT",EDGE,{"derivedFrom":sQuery(id+"F16.wireOp",EDGE,"E79.0")}),-1.0]])]});
            var Q2;
            Q2=makeQuery(id+"F16.imprint","IMPRINT",FACE,{"disambiguationData":[TD([[makeQuery(id+"F16.imprint","IMPRINT",EDGE,{"derivedFrom":sQuery(id+"F16.wireOp",EDGE,"E88.MirrorCS")}),-1.0]])]});
            var Q3;
            Q3=makeQuery(id+"F2.opExtrude","CAP_FACE",FACE,{"disambiguationData":[OSD([sQuery(id+"F0.wireOp",EDGE,"E12"),sQuery(id+"F0.wireOp",EDGE,"E13"),sQuery(id+"F0.wireOp",EDGE,"E14"),sQuery(id+"F0.wireOp",EDGE,"E15"),sQuery(id+"F0.wireOp",EDGE,"E17.filletArc"),sQuery(id+"F0.wireOp",EDGE,"E18.filletArc"),sQuery(id+"F0.wireOp",EDGE,"E19.filletArc"),sQuery(id+"F0.wireOp",EDGE,"E20.filletArc"),sQuery(id+"F0.wireOp",EDGE,"E25.0"),sQuery(id+"F0.wireOp",EDGE,"E25.1"),sQuery(id+"F0.wireOp",EDGE,"E25.2"),sQuery(id+"F0.wireOp",EDGE,"E25.3"),sQuery(id+"F0.wireOp",EDGE,"E25.4"),sQuery(id+"F0.wireOp",EDGE,"E25.5"),sQuery(id+"F0.wireOp",EDGE,"E25.6"),sQuery(id+"F0.wireOp",EDGE,"E25.7")])],"isStart":false});
            extrude(context, id + "F17", {"entities" : qUnion([Q0, Q1, Q2]), "operationType" : NewBodyOperationType.ADD, "endBound" : BoundingType.UP_TO_SURFACE, "endBoundEntityFace" : qUnion([Q3]), "depth" : 25 * mm});
        }
    });
